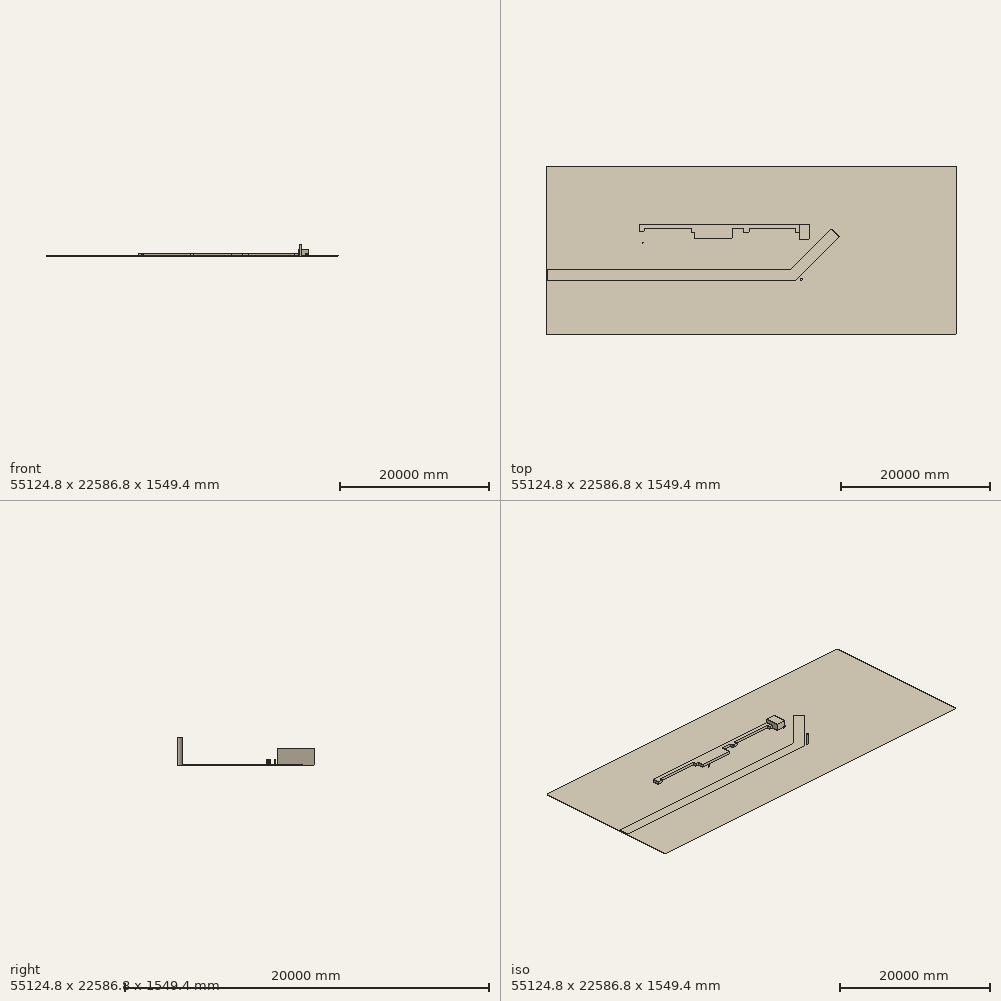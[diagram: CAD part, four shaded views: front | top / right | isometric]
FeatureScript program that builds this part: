
annotation { "Feature Type Name" : "Feature", "Feature Type Description" : "" }
export const myFeature = defineFeature(function(context is Context, id is Id, definition is map)
    precondition{}
    {
        {
            var Q0;
            Q0=qCreatedBy(makeId("Top.planeOp"),FACE);
            var sketch = newSketch(context, id + "F0", { "sketchPlane" : qUnion([Q0])});
            skLineSegment(sketch, "E0", {"start": v(-3920.42, 556.58) * mm, "end": v(-3920.42, 86.68) * mm});
            skLineSegment(sketch, "E1", {"start": v(-3920.42, 86.68) * mm, "end": v(-3158.42, 86.68) * mm});
            skLineSegment(sketch, "E2", {"start": v(-3158.42, 86.68) * mm, "end": v(-3158.42, 469.9) * mm});
            skLineSegment(sketch, "E3", {"start": v(-3158.42, 469.9) * mm, "end": v(3102.68, 469.9) * mm});
            skLineSegment(sketch, "E4", {"start": v(3102.68, 469.9) * mm, "end": v(3102.68, 0) * mm});
            skLineSegment(sketch, "E5", {"start": v(3102.68, 0) * mm, "end": v(3572.58, 0) * mm});
            skLineSegment(sketch, "E6", {"start": v(3572.58, 0) * mm, "end": v(3572.58, -850.9) * mm});
            skLineSegment(sketch, "E7", {"start": v(3572.58, -850.9) * mm, "end": v(8601.78, -850.9) * mm});
            skLineSegment(sketch, "E8", {"start": v(8601.78, -850.9) * mm, "end": v(8601.78, 469.9) * mm});
            skLineSegment(sketch, "E9", {"start": v(8601.78, 469.9) * mm, "end": v(10125.78, 469.9) * mm});
            skLineSegment(sketch, "E10", {"start": v(10125.78, 469.9) * mm, "end": v(10125.78, 0) * mm});
            skLineSegment(sketch, "E11", {"start": v(10125.78, 0) * mm, "end": v(10887.78, 0) * mm});
            skLineSegment(sketch, "E12", {"start": v(10887.78, 0) * mm, "end": v(10887.78, 469.9) * mm});
            skLineSegment(sketch, "E13", {"start": v(10887.78, 469.9) * mm, "end": v(17136.18, 469.9) * mm});
            skLineSegment(sketch, "E14", {"start": v(17136.18, 469.9) * mm, "end": v(17136.18, 0) * mm});
            skLineSegment(sketch, "E15", {"start": v(17136.18, 0) * mm, "end": v(17606.08, 0) * mm});
            skLineSegment(sketch, "E16", {"start": v(17606.08, 0) * mm, "end": v(17606.08, -914.4) * mm});
            skLineSegment(sketch, "E17", {"start": v(17606.08, -914.4) * mm, "end": v(19015.78, -914.4) * mm});
            skLineSegment(sketch, "E18", {"start": v(19015.78, -914.4) * mm, "end": v(19015.78, 469.9) * mm});
            skLineSegment(sketch, "E19", {"start": v(-3920.42, 556.58) * mm, "end": v(-3920.42, 1079.5) * mm});
            skLineSegment(sketch, "E20", {"start": v(-3920.42, 1079.5) * mm, "end": v(19015.78, 1079.5) * mm});
            skLineSegment(sketch, "E21", {"start": v(19015.78, 1079.5) * mm, "end": v(19015.78, 469.9) * mm});
            skSolve(sketch);
        }
        {
            var Q0;
            Q0=qCreatedBy(makeId("Top.planeOp"),FACE);
            var sketch = newSketch(context, id + "F1", { "sketchPlane" : qUnion([Q0])});
            skLineSegment(sketch, "E22.bottom", {"start": v(-16378.08, 8867.68) * mm, "end": v(38746.72, 8867.68) * mm});
            skLineSegment(sketch, "E22.top", {"start": v(-16378.08, -13719.12) * mm, "end": v(38746.72, -13719.12) * mm});
            skLineSegment(sketch, "E22.left", {"start": v(-16378.08, 8867.68) * mm, "end": v(-16378.08, -13719.12) * mm});
            skLineSegment(sketch, "E22.right", {"start": v(38746.72, 8867.68) * mm, "end": v(38746.72, -13719.12) * mm});
            skSolve(sketch);
        }
        {
            var Q0;
            Q0=qCreatedBy(makeId("Top.planeOp"),FACE);
            var sketch = newSketch(context, id + "F2", { "sketchPlane" : qUnion([Q0])});
            skLineSegment(sketch, "E23", {"start": v(8601.78, -4965.7) * mm, "end": v(-16214, -4965.7) * mm});
            skLineSegment(sketch, "E24", {"start": v(8601.78, -4965.7) * mm, "end": v(16523.94, -4965.7) * mm});
            skLineSegment(sketch, "E25", {"start": v(16528.43, -4963.84) * mm, "end": v(21914.73, 422.45) * mm});
            skLineSegment(sketch, "E26.0", {"start": v(8601.78, -6464.3) * mm, "end": v(-16214, -6464.3) * mm});
            skLineSegment(sketch, "E27.0", {"start": v(8601.78, -6464.3) * mm, "end": v(17147.32, -6464.3) * mm});
            skLineSegment(sketch, "E28.0", {"start": v(17147.32, -6464.3) * mm, "end": v(22974.4, -637.22) * mm});
            skPoint(sketch, "E29.visualSharp", {"position": v(16526.58, -4965.7) * mm});
            skArc(sketch, "E29.filletArc", {"start": v(16523.94, -4965.7) * mm, "mid": v(16526.37, -4965.22) * mm, "end": v(16528.43, -4963.84) * mm});
            skLineSegment(sketch, "E30", {"start": v(-16214, -4965.7) * mm, "end": v(-16214, -6464.3) * mm});
            skLineSegment(sketch, "E31", {"start": v(21914.73, 422.45) * mm, "end": v(22974.4, -637.22) * mm});
            skSolve(sketch);
        }
        {
            var Q0;
            Q0=makeQuery(id+"F1.imprint","IMPRINT",FACE,{"disambiguationData":[TD([[makeQuery(id+"F1.imprint","IMPRINT",EDGE,{"derivedFrom":sQuery(id+"F1.wireOp",EDGE,"E22.bottom")}),-1.0]])]});
            extrude(context, id + "F3", {"entities" : qUnion([Q0]), "oppositeDirection" : true, "depth" : 25.4 * mm, "offsetDistance" : 25.4 * mm});
        }
        {
            var Q0;
            Q0 = qSketchRegion(id + "F0", true);
            extrude(context, id + "F4", {"entities" : qUnion([Q0]), "operationType" : NewBodyOperationType.ADD, "depth" : 406.4 * mm, "offsetDistance" : 25.4 * mm});
        }
        {
            var Q0;
            Q0=makeQuery(id+"F2.imprint","IMPRINT",FACE,{"disambiguationData":[TD([[makeQuery(id+"F2.imprint","IMPRINT",EDGE,{"derivedFrom":sQuery(id+"F2.wireOp",EDGE,"E23")}),1.0]])]});
            extrude(context, id + "F5", {"entities" : qUnion([Q0]), "operationType" : NewBodyOperationType.ADD, "depth" : 25.4 * mm, "offsetDistance" : 25.4 * mm});
        }
        {
            var Q0;
            Q0=makeQuery(id+"F4.opExtrude","CAP_FACE",FACE,{"disambiguationData":[OSD([sQuery(id+"F0.wireOp",EDGE,"E0"),sQuery(id+"F0.wireOp",EDGE,"E1"),sQuery(id+"F0.wireOp",EDGE,"E2"),sQuery(id+"F0.wireOp",EDGE,"E3"),sQuery(id+"F0.wireOp",EDGE,"E4"),sQuery(id+"F0.wireOp",EDGE,"E5"),sQuery(id+"F0.wireOp",EDGE,"E6"),sQuery(id+"F0.wireOp",EDGE,"E7"),sQuery(id+"F0.wireOp",EDGE,"E8"),sQuery(id+"F0.wireOp",EDGE,"E9"),sQuery(id+"F0.wireOp",EDGE,"E10"),sQuery(id+"F0.wireOp",EDGE,"E11"),sQuery(id+"F0.wireOp",EDGE,"E12"),sQuery(id+"F0.wireOp",EDGE,"E13"),sQuery(id+"F0.wireOp",EDGE,"E14"),sQuery(id+"F0.wireOp",EDGE,"E15"),sQuery(id+"F0.wireOp",EDGE,"E16"),sQuery(id+"F0.wireOp",EDGE,"E17"),sQuery(id+"F0.wireOp",EDGE,"E18"),sQuery(id+"F0.wireOp",EDGE,"E19"),sQuery(id+"F0.wireOp",EDGE,"E20"),sQuery(id+"F0.wireOp",EDGE,"E21")])],"isStart":false});
            var sketch = newSketch(context, id + "F6", { "sketchPlane" : qUnion([Q0])});
            skLineSegment(sketch, "E32.bottom", {"start": v(19015.78, -914.4) * mm, "end": v(17606.08, -914.4) * mm});
            skLineSegment(sketch, "E32.left", {"start": v(19015.78, -914.4) * mm, "end": v(19015.78, 0) * mm});
            skLineSegment(sketch, "E32.right", {"start": v(17606.08, -914.4) * mm, "end": v(17606.08, 0) * mm});
            skLineSegment(sketch, "E33.top", {"start": v(17606.08, 1079.5) * mm, "end": v(19015.78, 1079.5) * mm});
            skLineSegment(sketch, "E33.left", {"start": v(17606.08, 0) * mm, "end": v(17606.08, 1079.5) * mm});
            skLineSegment(sketch, "E33.right", {"start": v(19015.78, 0) * mm, "end": v(19015.78, 1079.5) * mm});
            skSolve(sketch);
        }
        {
            var Q0;
            Q0 = qSketchRegion(id + "F6", true);
            extrude(context, id + "F7", {"entities" : qUnion([Q0]), "operationType" : NewBodyOperationType.ADD, "depth" : 533.4 * mm, "offsetDistance" : 25.4 * mm});
        }
        {
            var Q0;
            Q0=makeQuery(id+"F3.opExtrude","CAP_FACE",FACE,{"disambiguationData":[OSD([sQuery(id+"F1.wireOp",EDGE,"E22.bottom"),sQuery(id+"F1.wireOp",EDGE,"E22.top"),sQuery(id+"F1.wireOp",EDGE,"E22.left"),sQuery(id+"F1.wireOp",EDGE,"E22.right")])],"isStart":true});
            var sketch = newSketch(context, id + "F8", { "sketchPlane" : qUnion([Q0])});
            skCircle(sketch, "E34", {"center": v(4080.58, -1358.9) * mm, "radius": 25.4 * mm});
            skCircle(sketch, "E35.1.0.0", {"center": v(4207.58, -1358.9) * mm, "radius": 25.4 * mm});
            skCircle(sketch, "E35.2.0.0", {"center": v(4334.58, -1358.9) * mm, "radius": 25.4 * mm});
            skCircle(sketch, "E35.3.0.0", {"center": v(4461.58, -1358.9) * mm, "radius": 25.4 * mm});
            skLineSegment(sketch, "E35.direction1", {"start": v(4080.58, -1358.9) * mm, "end": v(4207.58, -1358.9) * mm, "construction": true});
            skSolve(sketch);
        }
        {
            var Q0;
            Q0 = qSketchRegion(id + "F8", true);
            extrude(context, id + "F9", {"entities" : qUnion([Q0]), "operationType" : NewBodyOperationType.ADD, "depth" : 304.8 * mm, "offsetDistance" : 25.4 * mm});
        }
        {
            var Q0;
            Q0=makeQuery(id+"F3.opExtrude","CAP_FACE",FACE,{"disambiguationData":[OSD([sQuery(id+"F1.wireOp",EDGE,"E22.bottom"),sQuery(id+"F1.wireOp",EDGE,"E22.top"),sQuery(id+"F1.wireOp",EDGE,"E22.left"),sQuery(id+"F1.wireOp",EDGE,"E22.right")])],"isStart":true});
            var sketch = newSketch(context, id + "F10", { "sketchPlane" : qUnion([Q0])});
            skCircle(sketch, "E36", {"center": v(-3300.83, -1601.87) * mm, "radius": 25.4 * mm});
            skCircle(sketch, "E37.0.1.0", {"center": v(-3300.83, -1507.9) * mm, "radius": 25.4 * mm});
            skCircle(sketch, "E37.0.2.0", {"center": v(-3300.83, -1413.91) * mm, "radius": 25.4 * mm});
            skCircle(sketch, "E37.1.0.0", {"center": v(-3392.27, -1601.87) * mm, "radius": 25.4 * mm});
            skCircle(sketch, "E37.1.1.0", {"center": v(-3392.27, -1507.9) * mm, "radius": 25.4 * mm});
            skCircle(sketch, "E37.1.2.0", {"center": v(-3392.27, -1413.91) * mm, "radius": 25.4 * mm});
            skCircle(sketch, "E37.2.0.0", {"center": v(-3483.71, -1601.87) * mm, "radius": 25.4 * mm});
            skCircle(sketch, "E37.2.1.0", {"center": v(-3483.71, -1507.9) * mm, "radius": 25.4 * mm});
            skCircle(sketch, "E37.2.2.0", {"center": v(-3483.71, -1413.91) * mm, "radius": 25.4 * mm});
            skLineSegment(sketch, "E37.direction1", {"start": v(-3300.83, -1601.87) * mm, "end": v(-3392.27, -1601.87) * mm, "construction": true});
            skLineSegment(sketch, "E37.direction2", {"start": v(-3300.83, -1601.87) * mm, "end": v(-3300.83, -1507.9) * mm, "construction": true});
            skSolve(sketch);
        }
        {
            var Q0;
            Q0 = qSketchRegion(id + "F10", true);
            extrude(context, id + "F11", {"entities" : qUnion([Q0]), "operationType" : NewBodyOperationType.ADD, "depth" : 304.8 * mm, "offsetDistance" : 25.4 * mm});
        }
        {
            var Q0;
            Q0=makeQuery(id+"F3.opExtrude","CAP_FACE",FACE,{"disambiguationData":[OSD([sQuery(id+"F1.wireOp",EDGE,"E22.bottom"),sQuery(id+"F1.wireOp",EDGE,"E22.top"),sQuery(id+"F1.wireOp",EDGE,"E22.left"),sQuery(id+"F1.wireOp",EDGE,"E22.right")])],"isStart":true});
            var sketch = newSketch(context, id + "F12", { "sketchPlane" : qUnion([Q0])});
            skCircle(sketch, "E38", {"center": v(18660.26, -1078.05) * mm, "radius": 25.4 * mm});
            skCircle(sketch, "E39.1.0.0", {"center": v(18759.32, -1078.05) * mm, "radius": 25.4 * mm});
            skCircle(sketch, "E39.2.0.0", {"center": v(18858.38, -1078.05) * mm, "radius": 25.4 * mm});
            skLineSegment(sketch, "E39.direction1", {"start": v(18660.26, -1078.05) * mm, "end": v(18759.32, -1078.05) * mm, "construction": true});
            skSolve(sketch);
        }
        {
            var Q0;
            Q0 = qSketchRegion(id + "F12", true);
            extrude(context, id + "F13", {"entities" : qUnion([Q0]), "operationType" : NewBodyOperationType.ADD, "depth" : 304.8 * mm, "offsetDistance" : 25.4 * mm});
        }
        {
            var Q0;
            Q0=makeQuery(id+"F3.opExtrude","CAP_FACE",FACE,{"disambiguationData":[OSD([sQuery(id+"F1.wireOp",EDGE,"E22.bottom"),sQuery(id+"F1.wireOp",EDGE,"E22.top"),sQuery(id+"F1.wireOp",EDGE,"E22.left"),sQuery(id+"F1.wireOp",EDGE,"E22.right")])],"isStart":true});
            var sketch = newSketch(context, id + "F14", { "sketchPlane" : qUnion([Q0])});
            skCircle(sketch, "E40", {"center": v(10230.72, -71.71) * mm, "radius": 25.4 * mm});
            skSolve(sketch);
        }
        {
            var Q0;
            Q0 = qSketchRegion(id + "F14", true);
            extrude(context, id + "F15", {"entities" : qUnion([Q0]), "operationType" : NewBodyOperationType.ADD, "depth" : 304.8 * mm, "offsetDistance" : 25.4 * mm});
        }
        {
            var Q0;
            Q0=makeQuery(id+"F3.opExtrude","CAP_FACE",FACE,{"disambiguationData":[OSD([sQuery(id+"F1.wireOp",EDGE,"E22.bottom"),sQuery(id+"F1.wireOp",EDGE,"E22.top"),sQuery(id+"F1.wireOp",EDGE,"E22.left"),sQuery(id+"F1.wireOp",EDGE,"E22.right")])],"isStart":true});
            var sketch = newSketch(context, id + "F16", { "sketchPlane" : qUnion([Q0])});
            skCircle(sketch, "E41", {"center": v(17954.74, -6310.4) * mm, "radius": 152.4 * mm});
            skSolve(sketch);
        }
        {
            var Q0;
            Q0 = qSketchRegion(id + "F16", true);
            extrude(context, id + "F17", {"entities" : qUnion([Q0]), "operationType" : NewBodyOperationType.ADD, "depth" : 1524 * mm, "offsetDistance" : 25.4 * mm});
        }
    });
